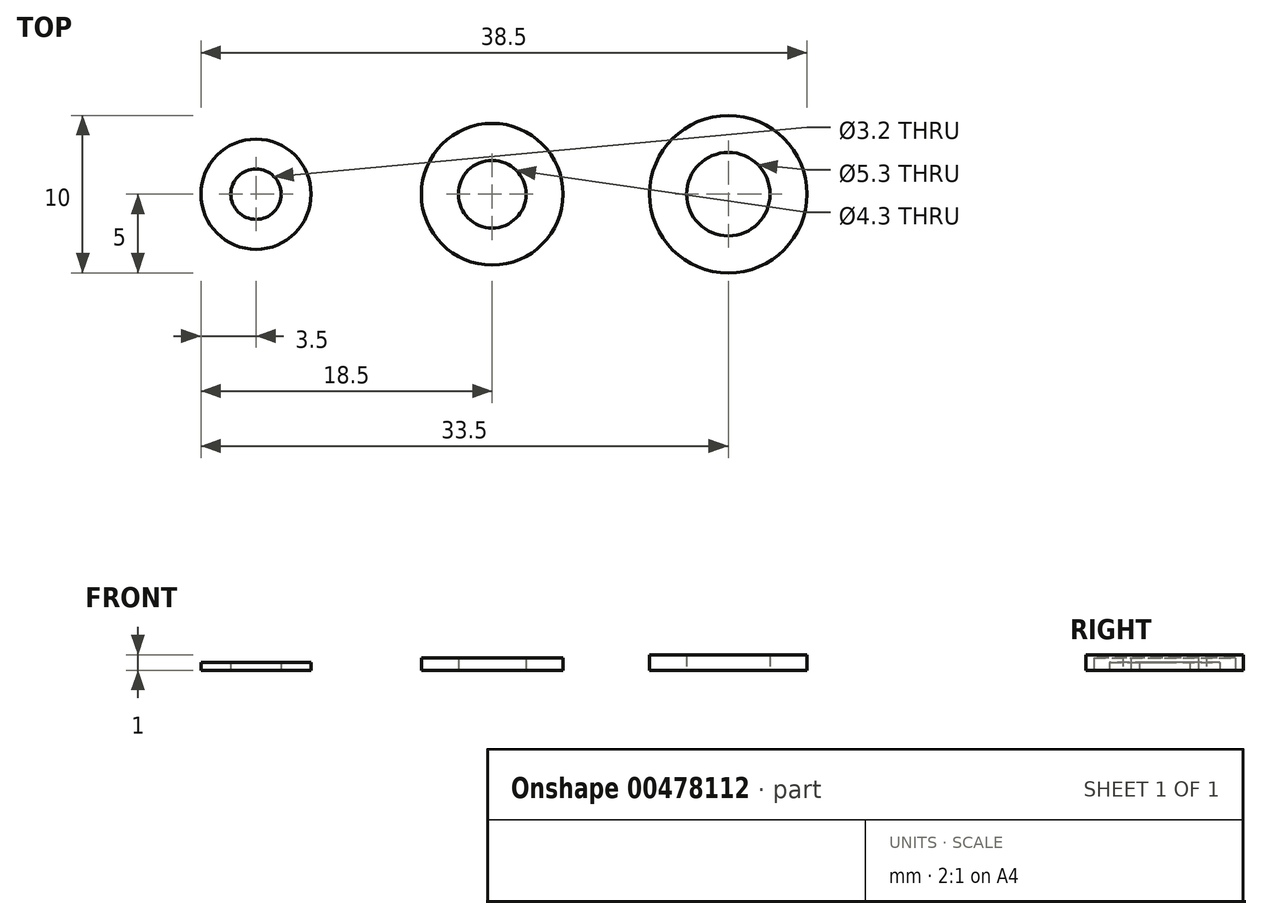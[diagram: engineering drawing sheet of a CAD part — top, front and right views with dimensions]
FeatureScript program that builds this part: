
annotation { "Feature Type Name" : "Feature", "Feature Type Description" : "" }
export const myFeature = defineFeature(function(context is Context, id is Id, definition is map)
    precondition{}
    {
        {
            var Q0;
            Q0=qCreatedBy(makeId("Top.planeOp"),FACE);
            var sketch = newSketch(context, id + "F0", { "sketchPlane" : qUnion([Q0])});
            skCircle(sketch, "E0", {"center": v(0, 0) * mm, "radius": 4.5 * mm});
            skCircle(sketch, "E1", {"center": v(0, 0) * mm, "radius": 2.15 * mm});
            skSolve(sketch);
        }
        {
            var Q0;
            Q0 = qSketchRegion(id + "F0", true);
            extrude(context, id + "F1", {"entities" : qUnion([Q0]), "depth" : .8 * mm});
        }
        {
            var Q0;
            Q0=qCreatedBy(makeId("Top.planeOp"),FACE);
            var sketch = newSketch(context, id + "F2", { "sketchPlane" : qUnion([Q0])});
            skCircle(sketch, "E2", {"center": v(0, 0) * mm, "radius": 5 * mm});
            skCircle(sketch, "E3", {"center": v(0, 0) * mm, "radius": 2.65 * mm});
            skSolve(sketch);
        }
        {
            var Q0;
            Q0 = qSketchRegion(id + "F2", true);
            extrude(context, id + "F3", {"entities" : qUnion([Q0]), "depth" : 1 * mm});
        }
        {
            var Q0;
            Q0=qCreatedBy(makeId("Top.planeOp"),FACE);
            var sketch = newSketch(context, id + "F4", { "sketchPlane" : qUnion([Q0])});
            skCircle(sketch, "E4", {"center": v(0, 0) * mm, "radius": 3.5 * mm});
            skCircle(sketch, "E5", {"center": v(0, 0) * mm, "radius": 1.6 * mm});
            skSolve(sketch);
        }
        {
            var Q0;
            Q0 = qSketchRegion(id + "F4", true);
            extrude(context, id + "F5", {"entities" : qUnion([Q0]), "depth" : .5 * mm});
        }
        {
            var Q0;
            Q0=makeQuery(id+"F1.opExtrude","SWEPT_BODY",BODY,{"disambiguationData":[OSD([sQuery(id+"F0.wireOp",EDGE,"E0"),sQuery(id+"F0.wireOp",EDGE,"E1")])]});
            transform(context, id + "F6", {"entities" : qUnion([Q0]), "transformType" : TransformType.TRANSLATION_3D, "dx" : 15 * mm, "dy" : 0 * mm, "dz" : 0 * mm, "makeCopy" : false});
        }
        {
            var Q0;
            Q0=makeQuery(id+"F3.opExtrude","SWEPT_BODY",BODY,{"disambiguationData":[OSD([sQuery(id+"F2.wireOp",EDGE,"E2"),sQuery(id+"F2.wireOp",EDGE,"E3")])]});
            transform(context, id + "F7", {"entities" : qUnion([Q0]), "transformType" : TransformType.TRANSLATION_3D, "dx" : 30 * mm, "dy" : 0 * mm, "dz" : 0 * mm, "makeCopy" : false});
        }
    });
